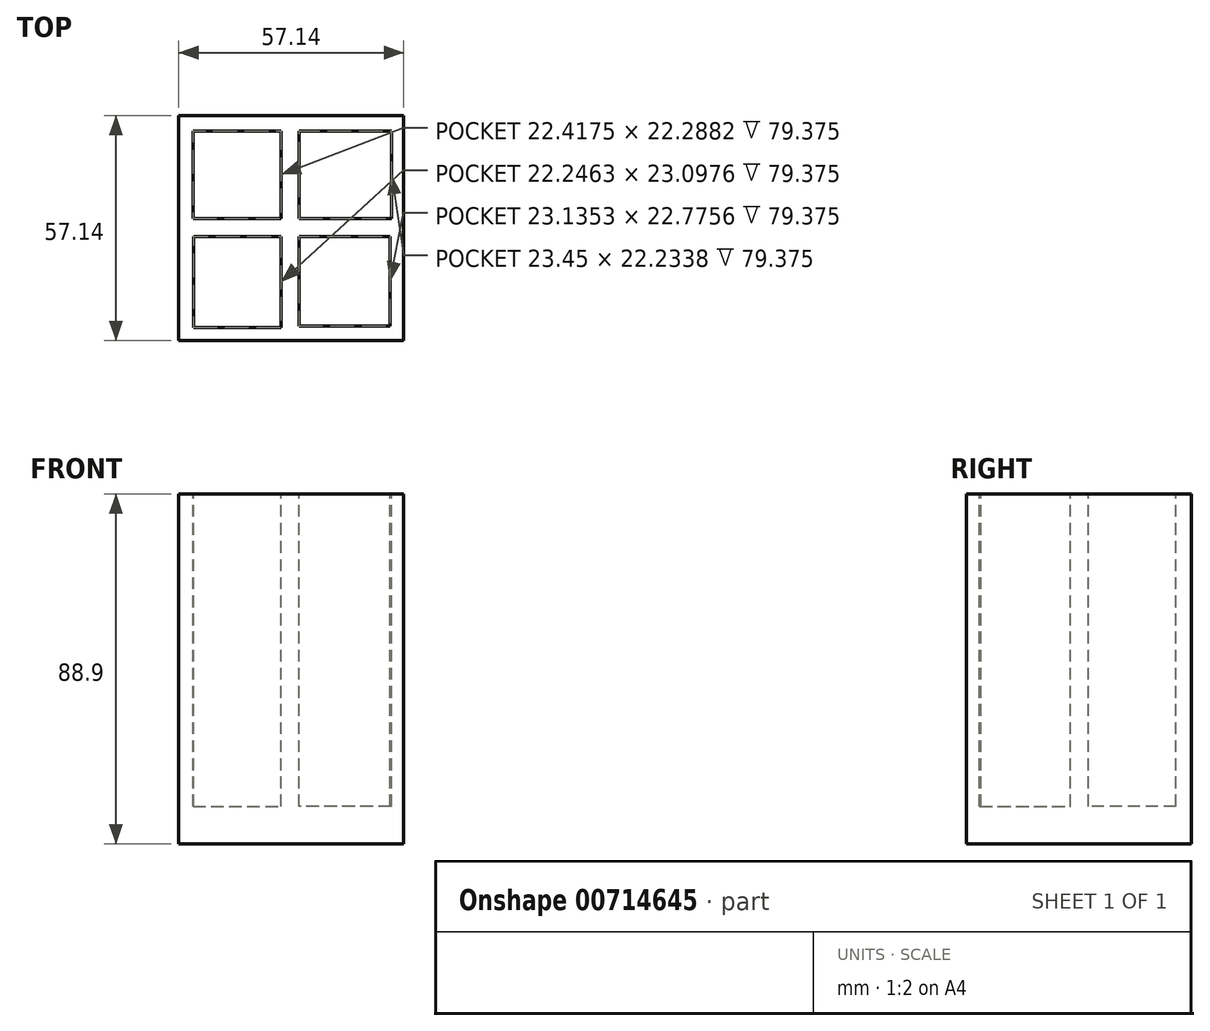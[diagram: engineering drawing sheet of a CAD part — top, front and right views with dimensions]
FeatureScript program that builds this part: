
annotation { "Feature Type Name" : "Feature", "Feature Type Description" : "" }
export const myFeature = defineFeature(function(context is Context, id is Id, definition is map)
    precondition{}
    {
        {
            var Q0;
            Q0=qCreatedBy(makeId("Top.planeOp"),FACE);
            var sketch = newSketch(context, id + "F0", { "sketchPlane" : qUnion([Q0])});
            skLineSegment(sketch, "E0.bottom", {"start": v(-28.57, -28.58) * mm, "end": v(28.58, -28.58) * mm});
            skLineSegment(sketch, "E0.top", {"start": v(-28.58, 28.57) * mm, "end": v(28.57, 28.57) * mm});
            skLineSegment(sketch, "E0.left", {"start": v(-28.57, -28.58) * mm, "end": v(-28.58, 28.57) * mm});
            skLineSegment(sketch, "E0.right", {"start": v(28.58, -28.58) * mm, "end": v(28.57, 28.57) * mm});
            skPoint(sketch, "E0.middle", {"position": v(0, 0) * mm});
            skSolve(sketch);
        }
        {
            var Q0;
            Q0=makeQuery(id+"F0.imprint","IMPRINT",FACE,{"disambiguationData":[TD([[makeQuery(id+"F0.imprint","IMPRINT",EDGE,{"derivedFrom":sQuery(id+"F0.wireOp",EDGE,"E0.bottom")}),1.0]])]});
            extrude(context, id + "F1", {"entities" : qUnion([Q0]), "depth" : 88.9 * mm, "offsetDistance" : 25.4 * mm});
        }
        {
            var Q0;
            Q0=makeQuery(id+"F1.opExtrude","CAP_FACE",FACE,{"disambiguationData":[OSD([sQuery(id+"F0.wireOp",EDGE,"E0.bottom"),sQuery(id+"F0.wireOp",EDGE,"E0.top"),sQuery(id+"F0.wireOp",EDGE,"E0.left"),sQuery(id+"F0.wireOp",EDGE,"E0.right")])],"isStart":false});
            var sketch = newSketch(context, id + "F2", { "sketchPlane" : qUnion([Q0])});
            skLineSegment(sketch, "E1.bottom", {"start": v(28.58, -28.58) * mm, "end": v(25.4, -28.58) * mm});
            skLineSegment(sketch, "E1.top", {"start": v(28.58, 28.57) * mm, "end": v(25.4, 28.57) * mm});
            skLineSegment(sketch, "E1.left", {"start": v(28.58, -28.58) * mm, "end": v(28.58, 28.57) * mm});
            skLineSegment(sketch, "E1.right", {"start": v(25.4, -28.58) * mm, "end": v(25.4, 28.57) * mm});
            skLineSegment(sketch, "E2.bottom", {"start": v(25.4, -28.58) * mm, "end": v(-28.57, -28.58) * mm});
            skLineSegment(sketch, "E2.top", {"start": v(25.4, -25.4) * mm, "end": v(-28.57, -25.4) * mm});
            skLineSegment(sketch, "E2.left", {"start": v(25.4, -28.58) * mm, "end": v(25.4, -25.4) * mm});
            skLineSegment(sketch, "E2.right", {"start": v(-28.57, -28.58) * mm, "end": v(-28.57, -25.4) * mm});
            skSolve(sketch);
        }
        {
            var Q0;
            {var subQ0=sQuery(id+"F2.wireOp",EDGE,"E1.right");Q0=makeQuery(id+"F2.imprint","IMPRINT",FACE,{"disambiguationData":[TD([[makeQuery(id+"F2.imprint","IMPRINT",EDGE,{"derivedFrom":subQ0}),1.0]])]});}
            var sketch = newSketch(context, id + "F3", { "sketchPlane" : qUnion([Q0])});
            skLineSegment(sketch, "E3.bottom", {"start": v(-24.98, 24.69) * mm, "end": v(-2.56, 24.69) * mm});
            skLineSegment(sketch, "E3.top", {"start": v(-24.98, 2.4) * mm, "end": v(-2.56, 2.4) * mm});
            skLineSegment(sketch, "E3.left", {"start": v(-24.98, 24.69) * mm, "end": v(-24.98, 2.4) * mm});
            skLineSegment(sketch, "E3.right", {"start": v(-2.56, 24.69) * mm, "end": v(-2.56, 2.4) * mm});
            skLineSegment(sketch, "E4.bottom", {"start": v(25.43, 24.63) * mm, "end": v(1.98, 24.63) * mm});
            skLineSegment(sketch, "E4.top", {"start": v(25.43, 2.4) * mm, "end": v(1.98, 2.4) * mm});
            skLineSegment(sketch, "E4.left", {"start": v(25.43, 24.63) * mm, "end": v(25.43, 2.4) * mm});
            skLineSegment(sketch, "E4.right", {"start": v(1.98, 24.63) * mm, "end": v(1.98, 2.4) * mm});
            skLineSegment(sketch, "E5.bottom", {"start": v(-24.8, -25.26) * mm, "end": v(-2.56, -25.26) * mm});
            skLineSegment(sketch, "E5.top", {"start": v(-24.8, -2.16) * mm, "end": v(-2.56, -2.16) * mm});
            skLineSegment(sketch, "E5.left", {"start": v(-24.8, -25.26) * mm, "end": v(-24.8, -2.16) * mm});
            skLineSegment(sketch, "E5.right", {"start": v(-2.56, -25.26) * mm, "end": v(-2.56, -2.16) * mm});
            skLineSegment(sketch, "E6.bottom", {"start": v(25.11, -24.94) * mm, "end": v(1.98, -24.94) * mm});
            skLineSegment(sketch, "E6.top", {"start": v(25.11, -2.16) * mm, "end": v(1.98, -2.16) * mm});
            skLineSegment(sketch, "E6.left", {"start": v(25.11, -24.94) * mm, "end": v(25.11, -2.16) * mm});
            skLineSegment(sketch, "E6.right", {"start": v(1.98, -24.94) * mm, "end": v(1.98, -2.16) * mm});
            skSolve(sketch);
        }
        {
            var Q0;
            Q0 = qSketchRegion(id + "F3", true);
            extrude(context, id + "F4", {"entities" : qUnion([Q0]), "operationType" : NewBodyOperationType.REMOVE, "oppositeDirection" : true, "depth" : 79.38 * mm, "offsetDistance" : 25.4 * mm});
        }
    });
